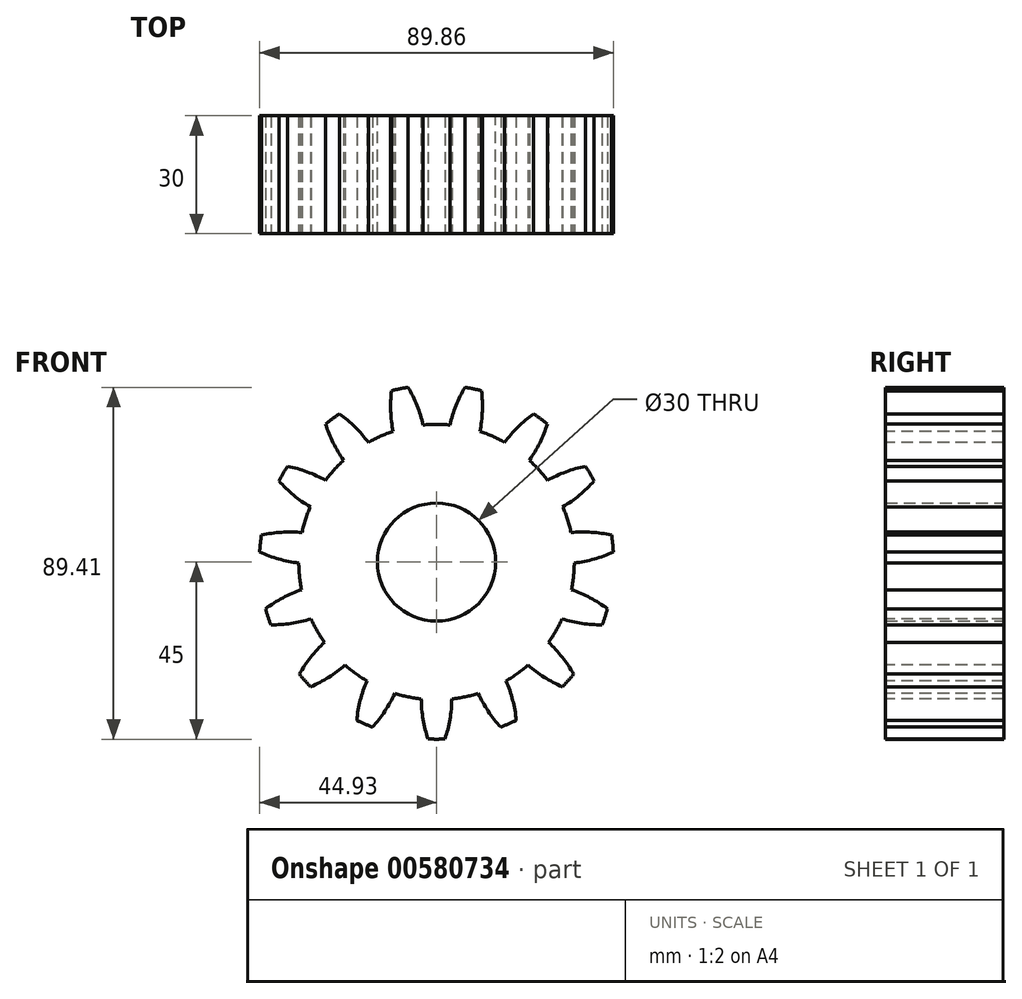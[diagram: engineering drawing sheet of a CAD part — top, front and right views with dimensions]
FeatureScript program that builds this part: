
annotation { "Feature Type Name" : "Feature", "Feature Type Description" : "" }
export const myFeature = defineFeature(function(context is Context, id is Id, definition is map)
    precondition{}
    {
        {
            var Q0;
            Q0=qCreatedBy(makeId("Front.planeOp"),FACE);
            var sketch = newSketch(context, id + "F0", { "sketchPlane" : qUnion([Q0])});
            skCircle(sketch, "E0", {"center": v(0, 0) * mm, "radius": 45 * mm});
            skCircle(sketch, "E1", {"center": v(0, 0) * mm, "radius": 15 * mm});
            skSolve(sketch);
        }
        {
            var Q0;
            Q0 = qSketchRegion(id + "F0", true);
            extrude(context, id + "F1", {"entities" : qUnion([Q0]), "depth" : 30 * mm, "offsetDistance" : 25 * mm});
        }
        {
            var Q0;
            Q0=makeQuery(id+"F1.opExtrude","CAP_FACE",FACE,{"disambiguationData":[OSD([sQuery(id+"F0.wireOp",EDGE,"E0"),sQuery(id+"F0.wireOp",EDGE,"E1")])],"isStart":false});
            var sketch = newSketch(context, id + "F2", { "sketchPlane" : qUnion([Q0])});
            skArc(sketch, "E2", {"start": v(10.44, 48.9) * mm, "mid": v(0, 50) * mm, "end": v(-10.44, 48.9) * mm});
            skArc(sketch, "E3", {"start": v(3.43, 34.83) * mm, "mid": v(0, 35) * mm, "end": v(-3.43, 34.83) * mm});
            skPoint(sketch, "E4", {"position": v(0, 27.6) * mm});
            skArc(sketch, "E5", {"start": v(10.44, 48.9) * mm, "mid": v(6.09, 42.29) * mm, "end": v(3.43, 34.83) * mm});
            skArc(sketch, "E6.MirrorC", {"start": v(-10.44, 48.9) * mm, "mid": v(-6.09, 42.29) * mm, "end": v(-3.43, 34.83) * mm});
            skArc(sketch, "E7.1.0", {"start": v(-10.35, 48.92) * mm, "mid": v(-20.34, 45.68) * mm, "end": v(-29.43, 40.42) * mm});
            skArc(sketch, "E7.1.1", {"start": v(-10.35, 48.92) * mm, "mid": v(-11.64, 41.1) * mm, "end": v(-11.03, 33.22) * mm});
            skArc(sketch, "E7.1.2", {"start": v(-11.03, 33.22) * mm, "mid": v(-14.24, 31.97) * mm, "end": v(-17.3, 30.42) * mm});
            skArc(sketch, "E7.1.3", {"start": v(-29.43, 40.42) * mm, "mid": v(-22.76, 36.16) * mm, "end": v(-17.3, 30.42) * mm});
            skArc(sketch, "E7.2.0", {"start": v(-29.35, 40.48) * mm, "mid": v(-37.16, 33.46) * mm, "end": v(-43.33, 24.96) * mm});
            skArc(sketch, "E7.2.1", {"start": v(-29.35, 40.48) * mm, "mid": v(-27.36, 32.82) * mm, "end": v(-23.59, 25.86) * mm});
            skArc(sketch, "E7.2.2", {"start": v(-23.59, 25.86) * mm, "mid": v(-26.01, 23.42) * mm, "end": v(-28.18, 20.76) * mm});
            skArc(sketch, "E7.2.3", {"start": v(-43.33, 24.96) * mm, "mid": v(-35.5, 23.77) * mm, "end": v(-28.18, 20.76) * mm});
            skArc(sketch, "E7.3.0", {"start": v(-43.28, 25.04) * mm, "mid": v(-47.55, 15.45) * mm, "end": v(-49.73, 5.18) * mm});
            skArc(sketch, "E7.3.1", {"start": v(-43.28, 25.04) * mm, "mid": v(-38.34, 18.86) * mm, "end": v(-32.07, 14.03) * mm});
            skArc(sketch, "E7.3.2", {"start": v(-32.07, 14.03) * mm, "mid": v(-33.29, 10.82) * mm, "end": v(-34.19, 7.5) * mm});
            skArc(sketch, "E7.3.3", {"start": v(-49.73, 5.18) * mm, "mid": v(-42.1, 7.28) * mm, "end": v(-34.19, 7.5) * mm});
            skArc(sketch, "E7.4.0", {"start": v(-49.72, 5.27) * mm, "mid": v(-49.73, -5.23) * mm, "end": v(-47.54, -15.5) * mm});
            skArc(sketch, "E7.4.1", {"start": v(-49.72, 5.27) * mm, "mid": v(-42.7, 1.63) * mm, "end": v(-35, -0.23) * mm});
            skArc(sketch, "E7.4.2", {"start": v(-35, -0.23) * mm, "mid": v(-34.8, -3.66) * mm, "end": v(-34.28, -7.05) * mm});
            skArc(sketch, "E7.4.3", {"start": v(-47.54, -15.5) * mm, "mid": v(-41.42, -10.47) * mm, "end": v(-34.28, -7.05) * mm});
            skArc(sketch, "E7.5.0", {"start": v(-47.57, -15.4) * mm, "mid": v(-43.3, -25) * mm, "end": v(-37.12, -33.5) * mm});
            skArc(sketch, "E7.5.1", {"start": v(-47.57, -15.4) * mm, "mid": v(-39.67, -15.87) * mm, "end": v(-31.88, -14.44) * mm});
            skArc(sketch, "E7.5.2", {"start": v(-31.88, -14.44) * mm, "mid": v(-30.31, -17.5) * mm, "end": v(-28.45, -20.39) * mm});
            skArc(sketch, "E7.5.3", {"start": v(-37.12, -33.5) * mm, "mid": v(-33.58, -26.41) * mm, "end": v(-28.45, -20.39) * mm});
            skArc(sketch, "E7.6.0", {"start": v(-37.19, -33.42) * mm, "mid": v(-29.39, -40.45) * mm, "end": v(-20.3, -45.7) * mm});
            skArc(sketch, "E7.6.1", {"start": v(-37.19, -33.42) * mm, "mid": v(-29.78, -30.64) * mm, "end": v(-23.25, -26.16) * mm});
            skArc(sketch, "E7.6.2", {"start": v(-23.25, -26.16) * mm, "mid": v(-20.57, -28.32) * mm, "end": v(-17.7, -30.2) * mm});
            skArc(sketch, "E7.6.3", {"start": v(-20.3, -45.7) * mm, "mid": v(-19.93, -37.79) * mm, "end": v(-17.7, -30.2) * mm});
            skArc(sketch, "E7.7.0", {"start": v(-20.38, -45.66) * mm, "mid": v(-10.4, -48.9) * mm, "end": v(0.05, -50) * mm});
            skArc(sketch, "E7.7.1", {"start": v(-20.38, -45.66) * mm, "mid": v(-14.74, -40.1) * mm, "end": v(-10.6, -33.36) * mm});
            skArc(sketch, "E7.7.2", {"start": v(-10.6, -33.36) * mm, "mid": v(-7.28, -34.24) * mm, "end": v(-3.89, -34.78) * mm});
            skArc(sketch, "E7.7.3", {"start": v(0.05, -50) * mm, "mid": v(-2.84, -42.63) * mm, "end": v(-3.89, -34.78) * mm});
            skArc(sketch, "E7.8.0", {"start": v(-0.05, -50) * mm, "mid": v(10.4, -48.9) * mm, "end": v(20.38, -45.66) * mm});
            skArc(sketch, "E7.8.1", {"start": v(-0.05, -50) * mm, "mid": v(2.84, -42.63) * mm, "end": v(3.89, -34.78) * mm});
            skArc(sketch, "E7.8.2", {"start": v(3.89, -34.78) * mm, "mid": v(7.28, -34.24) * mm, "end": v(10.6, -33.36) * mm});
            skArc(sketch, "E7.8.3", {"start": v(20.38, -45.66) * mm, "mid": v(14.74, -40.1) * mm, "end": v(10.6, -33.36) * mm});
            skArc(sketch, "E7.9.0", {"start": v(20.3, -45.7) * mm, "mid": v(29.39, -40.45) * mm, "end": v(37.19, -33.42) * mm});
            skArc(sketch, "E7.9.1", {"start": v(20.3, -45.7) * mm, "mid": v(19.93, -37.79) * mm, "end": v(17.7, -30.2) * mm});
            skArc(sketch, "E7.9.2", {"start": v(17.7, -30.2) * mm, "mid": v(20.57, -28.32) * mm, "end": v(23.25, -26.16) * mm});
            skArc(sketch, "E7.9.3", {"start": v(37.19, -33.42) * mm, "mid": v(29.78, -30.64) * mm, "end": v(23.25, -26.16) * mm});
            skArc(sketch, "E7.10.0", {"start": v(37.12, -33.5) * mm, "mid": v(43.3, -25) * mm, "end": v(47.57, -15.4) * mm});
            skArc(sketch, "E7.10.1", {"start": v(37.12, -33.5) * mm, "mid": v(33.58, -26.41) * mm, "end": v(28.45, -20.39) * mm});
            skArc(sketch, "E7.10.2", {"start": v(28.45, -20.39) * mm, "mid": v(30.31, -17.5) * mm, "end": v(31.88, -14.44) * mm});
            skArc(sketch, "E7.10.3", {"start": v(47.57, -15.4) * mm, "mid": v(39.67, -15.87) * mm, "end": v(31.88, -14.44) * mm});
            skArc(sketch, "E7.11.0", {"start": v(47.54, -15.5) * mm, "mid": v(49.73, -5.23) * mm, "end": v(49.72, 5.27) * mm});
            skArc(sketch, "E7.11.1", {"start": v(47.54, -15.5) * mm, "mid": v(41.42, -10.47) * mm, "end": v(34.28, -7.05) * mm});
            skArc(sketch, "E7.11.2", {"start": v(34.28, -7.05) * mm, "mid": v(34.8, -3.66) * mm, "end": v(35, -0.23) * mm});
            skArc(sketch, "E7.11.3", {"start": v(49.72, 5.27) * mm, "mid": v(42.7, 1.63) * mm, "end": v(35, -0.23) * mm});
            skArc(sketch, "E7.12.0", {"start": v(49.73, 5.18) * mm, "mid": v(47.55, 15.45) * mm, "end": v(43.28, 25.04) * mm});
            skArc(sketch, "E7.12.1", {"start": v(49.73, 5.18) * mm, "mid": v(42.1, 7.28) * mm, "end": v(34.19, 7.5) * mm});
            skArc(sketch, "E7.12.2", {"start": v(34.19, 7.5) * mm, "mid": v(33.29, 10.82) * mm, "end": v(32.07, 14.03) * mm});
            skArc(sketch, "E7.12.3", {"start": v(43.28, 25.04) * mm, "mid": v(38.34, 18.86) * mm, "end": v(32.07, 14.03) * mm});
            skArc(sketch, "E7.13.0", {"start": v(43.33, 24.96) * mm, "mid": v(37.16, 33.46) * mm, "end": v(29.35, 40.48) * mm});
            skArc(sketch, "E7.13.1", {"start": v(43.33, 24.96) * mm, "mid": v(35.5, 23.77) * mm, "end": v(28.18, 20.76) * mm});
            skArc(sketch, "E7.13.2", {"start": v(28.18, 20.76) * mm, "mid": v(26.01, 23.42) * mm, "end": v(23.59, 25.86) * mm});
            skArc(sketch, "E7.13.3", {"start": v(29.35, 40.48) * mm, "mid": v(27.36, 32.82) * mm, "end": v(23.59, 25.86) * mm});
            skArc(sketch, "E8.3.14.0", {"start": v(29.43, 40.42) * mm, "mid": v(20.34, 45.68) * mm, "end": v(10.35, 48.92) * mm});
            skArc(sketch, "E8.4.14.0", {"start": v(29.43, 40.42) * mm, "mid": v(22.76, 36.16) * mm, "end": v(17.3, 30.42) * mm});
            skArc(sketch, "E8.8.14.0", {"start": v(17.3, 30.42) * mm, "mid": v(14.24, 31.97) * mm, "end": v(11.03, 33.22) * mm});
            skArc(sketch, "E8.12.14.0", {"start": v(10.35, 48.92) * mm, "mid": v(11.64, 41.1) * mm, "end": v(11.03, 33.22) * mm});
            skSolve(sketch);
        }
        {
            var Q0;
            Q0 = qSketchRegion(id + "F2", true);
            extrude(context, id + "F3", {"entities" : qUnion([Q0]), "operationType" : NewBodyOperationType.REMOVE, "oppositeDirection" : true, "depth" : 31 * mm, "offsetDistance" : 25 * mm});
        }
    });
